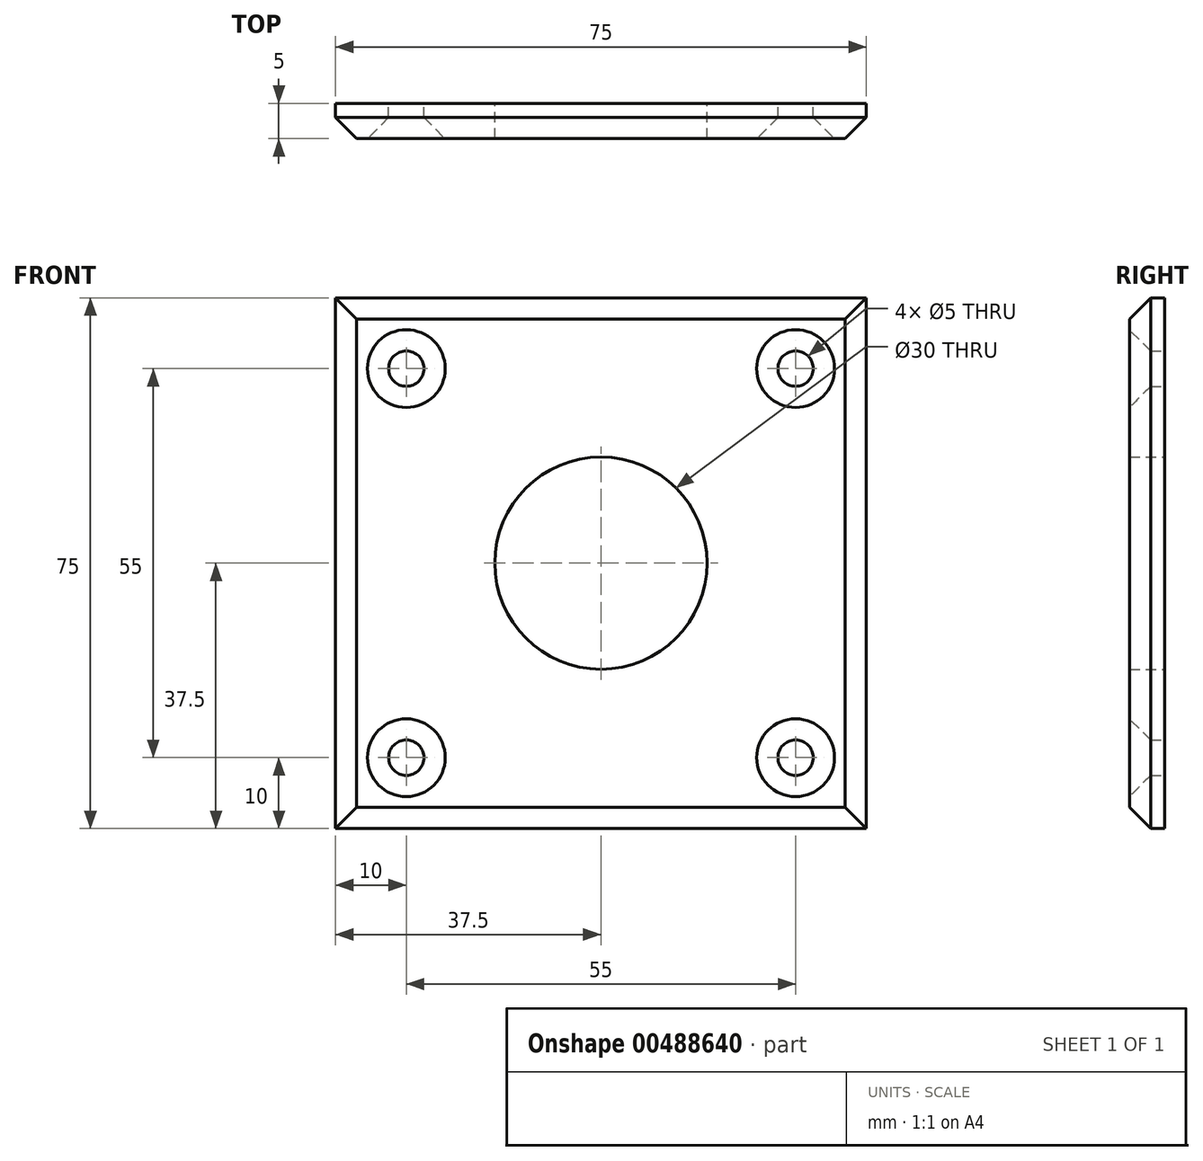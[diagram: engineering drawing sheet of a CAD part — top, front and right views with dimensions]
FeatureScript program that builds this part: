
annotation { "Feature Type Name" : "Feature", "Feature Type Description" : "" }
export const myFeature = defineFeature(function(context is Context, id is Id, definition is map)
    precondition{}
    {
        {
            var Q0;
            Q0=qCreatedBy(makeId("Front.planeOp"),FACE);
            var sketch = newSketch(context, id + "F0", { "sketchPlane" : qUnion([Q0])});
            skLineSegment(sketch, "E0.bottom", {"start": v(0, 0) * mm, "end": v(75, 0) * mm});
            skLineSegment(sketch, "E0.top", {"start": v(0, 75) * mm, "end": v(75, 75) * mm});
            skLineSegment(sketch, "E0.left", {"start": v(0, 0) * mm, "end": v(0, 75) * mm});
            skLineSegment(sketch, "E0.right", {"start": v(75, 0) * mm, "end": v(75, 75) * mm});
            skCircle(sketch, "E1", {"center": v(37.5, 37.5) * mm, "radius": 15 * mm});
            skCircle(sketch, "E2", {"center": v(10, 65) * mm, "radius": 2.5 * mm});
            skCircle(sketch, "E3", {"center": v(10, 10) * mm, "radius": 2.5 * mm});
            skCircle(sketch, "E4", {"center": v(65, 10) * mm, "radius": 2.5 * mm});
            skCircle(sketch, "E5", {"center": v(65, 65) * mm, "radius": 2.5 * mm});
            skSolve(sketch);
        }
        {
            var Q0;
            Q0 = qSketchRegion(id + "F0", true);
            extrude(context, id + "F1", {"entities" : qUnion([Q0]), "depth" : 5 * mm});
        }
        {
            var Q0;
            Q0=makeQuery(id+"F1.opExtrude","CAP_EDGE",EDGE,{"disambiguationData":[OSD([sQuery(id+"F0.wireOp",EDGE,"E0.right")])],"isStart":false});
            var Q1;
            Q1=makeQuery(id+"F1.opExtrude","CAP_EDGE",EDGE,{"disambiguationData":[OSD([sQuery(id+"F0.wireOp",EDGE,"E0.bottom")])],"isStart":false});
            var Q2;
            Q2=makeQuery(id+"F1.opExtrude","CAP_EDGE",EDGE,{"disambiguationData":[OSD([sQuery(id+"F0.wireOp",EDGE,"E0.top")])],"isStart":false});
            var Q3;
            Q3=makeQuery(id+"F1.opExtrude","CAP_EDGE",EDGE,{"disambiguationData":[OSD([sQuery(id+"F0.wireOp",EDGE,"E0.left")])],"isStart":false});
            var Q4;
            Q4=makeQuery(id+"F1.opExtrude","CAP_EDGE",EDGE,{"disambiguationData":[OSD([sQuery(id+"F0.wireOp",EDGE,"E2")])],"isStart":false});
            var Q5;
            Q5=makeQuery(id+"F1.opExtrude","CAP_EDGE",EDGE,{"disambiguationData":[OSD([sQuery(id+"F0.wireOp",EDGE,"E3")])],"isStart":false});
            var Q6;
            Q6=makeQuery(id+"F1.opExtrude","CAP_EDGE",EDGE,{"disambiguationData":[OSD([sQuery(id+"F0.wireOp",EDGE,"E4")])],"isStart":false});
            var Q7;
            Q7=makeQuery(id+"F1.opExtrude","CAP_EDGE",EDGE,{"disambiguationData":[OSD([sQuery(id+"F0.wireOp",EDGE,"E5")])],"isStart":false});
            chamfer(context, id + "F2", {"entities" : qUnion([Q0, Q1, Q2, Q3, Q4, Q5, Q6, Q7]), "width" : 3 * mm, "tangentPropagation" : true});
        }
    });
